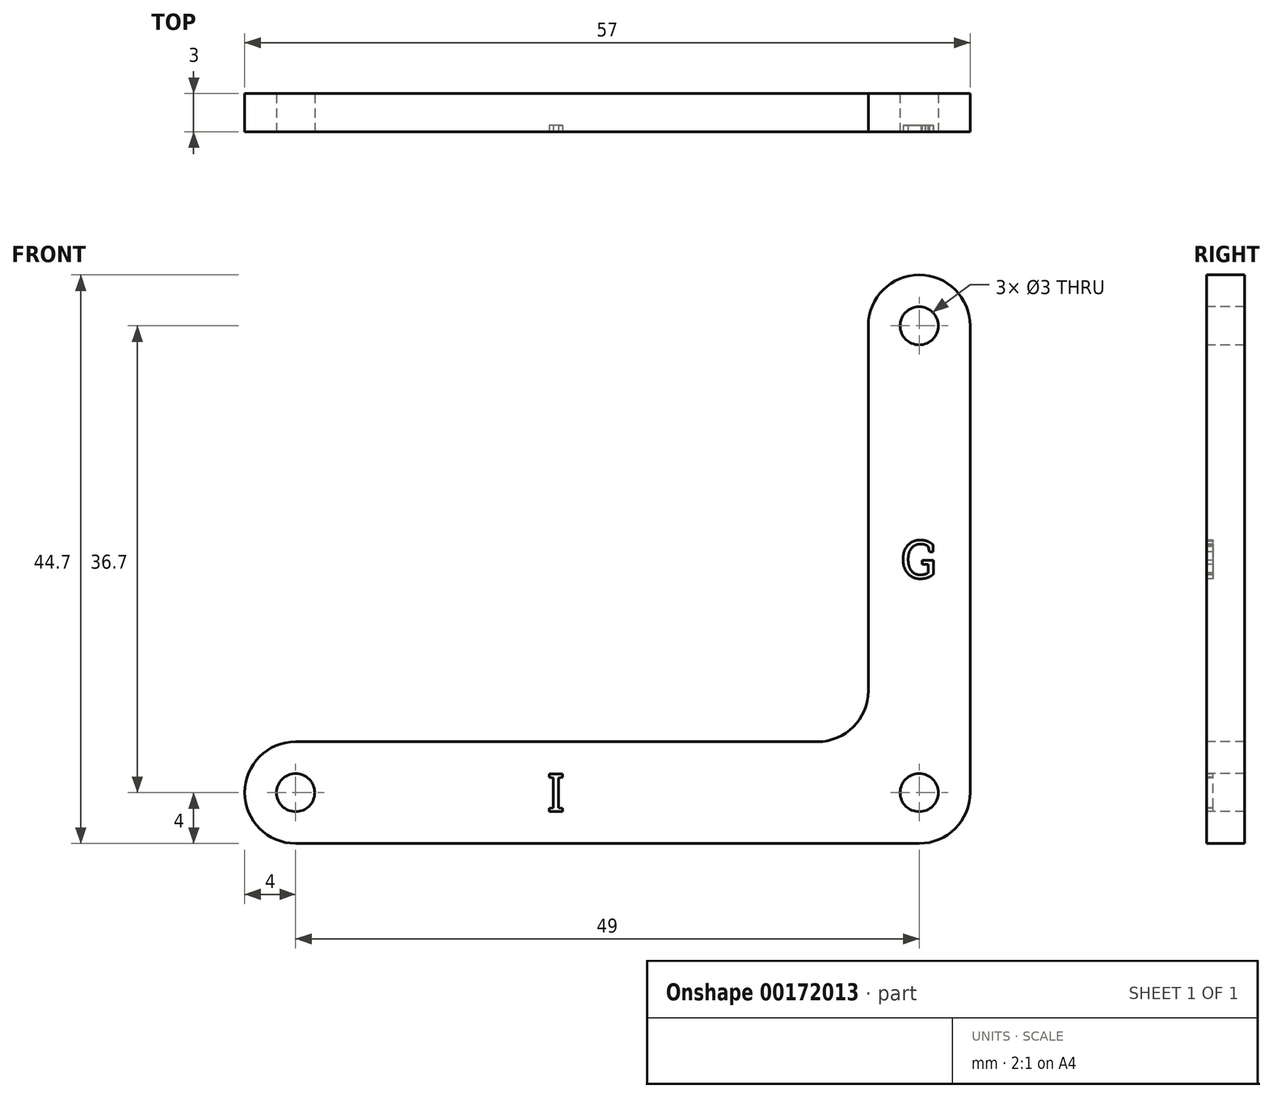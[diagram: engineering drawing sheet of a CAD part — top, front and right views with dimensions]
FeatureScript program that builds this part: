
annotation { "Feature Type Name" : "Feature", "Feature Type Description" : "" }
export const myFeature = defineFeature(function(context is Context, id is Id, definition is map)
    precondition{}
    {
        {
            assignVariable(context, id + "F0", {"name" : "Thickness", "anyValue" : 3});
        }
        {
            var Q0;
            Q0=qCreatedBy(makeId("Front.planeOp"),FACE);
            var sketch = newSketch(context, id + "F1", { "sketchPlane" : qUnion([Q0])});
            skCircle(sketch, "E0", {"center": v(-49, 0) * mm, "radius": 1.5 * mm});
            skCircle(sketch, "E1", {"center": v(0, 36.7) * mm, "radius": 1.5 * mm});
            skCircle(sketch, "E2", {"center": v(0, 0) * mm, "radius": 1.5 * mm});
            skArc(sketch, "E3", {"start": v(-49, 4) * mm, "mid": v(-53, 0) * mm, "end": v(-49, -4) * mm});
            skArc(sketch, "E4", {"start": v(4, 36.7) * mm, "mid": v(0, 40.7) * mm, "end": v(-4, 36.7) * mm});
            skArc(sketch, "E5", {"start": v(0, -4) * mm, "mid": v(2.83, -2.83) * mm, "end": v(4, 0) * mm});
            skArc(sketch, "E6", {"start": v(-8, 4) * mm, "mid": v(-5.17, 5.17) * mm, "end": v(-4, 8) * mm});
            skLineSegment(sketch, "E7", {"start": v(-49, 4) * mm, "end": v(-8, 4) * mm});
            skLineSegment(sketch, "E8", {"start": v(-4, 8) * mm, "end": v(-4, 36.7) * mm});
            skLineSegment(sketch, "E9", {"start": v(4, 36.7) * mm, "end": v(4, 0) * mm});
            skLineSegment(sketch, "E10", {"start": v(0, -4) * mm, "end": v(-49, -4) * mm});
            skSolve(sketch);
        }
        {
            var Q0;
            Q0=makeQuery(id+"F1.imprint","IMPRINT",FACE,{"disambiguationData":[TD([[makeQuery(id+"F1.imprint","IMPRINT",EDGE,{"derivedFrom":sQuery(id+"F1.wireOp",EDGE,"E0")}),-1.0]])]});
            extrude(context, id + "F2", {"entities" : qUnion([Q0]), "oppositeDirection" : true, "depth" : (getVariable(context, 'Thickness')) * mm});
        }
        {
            var Q0;
            Q0=qCreatedBy(makeId("Front.planeOp"),FACE);
            var sketch = newSketch(context, id + "F3", { "sketchPlane" : qUnion([Q0])});
            skText(sketch, "E11", { "text": "G", "fontName": "RobotoSlab-Regular.ttf"});
            skText(sketch, "E12", { "text": "I", "fontName": "RobotoSlab-Regular.ttf"});
            skLineSegment(sketch, "E13", {"start": v(-29.23, 0) * mm, "end": v(-27.77, 0) * mm, "construction": true});
            skLineSegment(sketch, "E14", {"start": v(1.38, 18.35) * mm, "end": v(4, 18.35) * mm, "construction": true});
            skLineSegment(sketch, "E15", {"start": v(-28.5, 1.5) * mm, "end": v(-28.5, 4) * mm, "construction": true});
            const initialGuessF3  = {"E11": [-0.00138, 0.01685, 1, 0, 0.003], "E12": [-0.02923, -0.0015, 1, 0, 0.003]};
            skSetInitialGuess(sketch, initialGuessF3);
            skSolve(sketch);
        }
        {
            assignVariable(context, id + "F4", {"name" : "DepthText", "anyValue" : .5});
        }
        {
            var Q0;
            Q0=qSketchRegion(id+"F3",true);
            extrude(context, id + "F5", {"entities" : qUnion([Q0]), "operationType" : NewBodyOperationType.REMOVE, "oppositeDirection" : true, "depth" : (getVariable(context, 'DepthText')) * mm});
        }
    });
